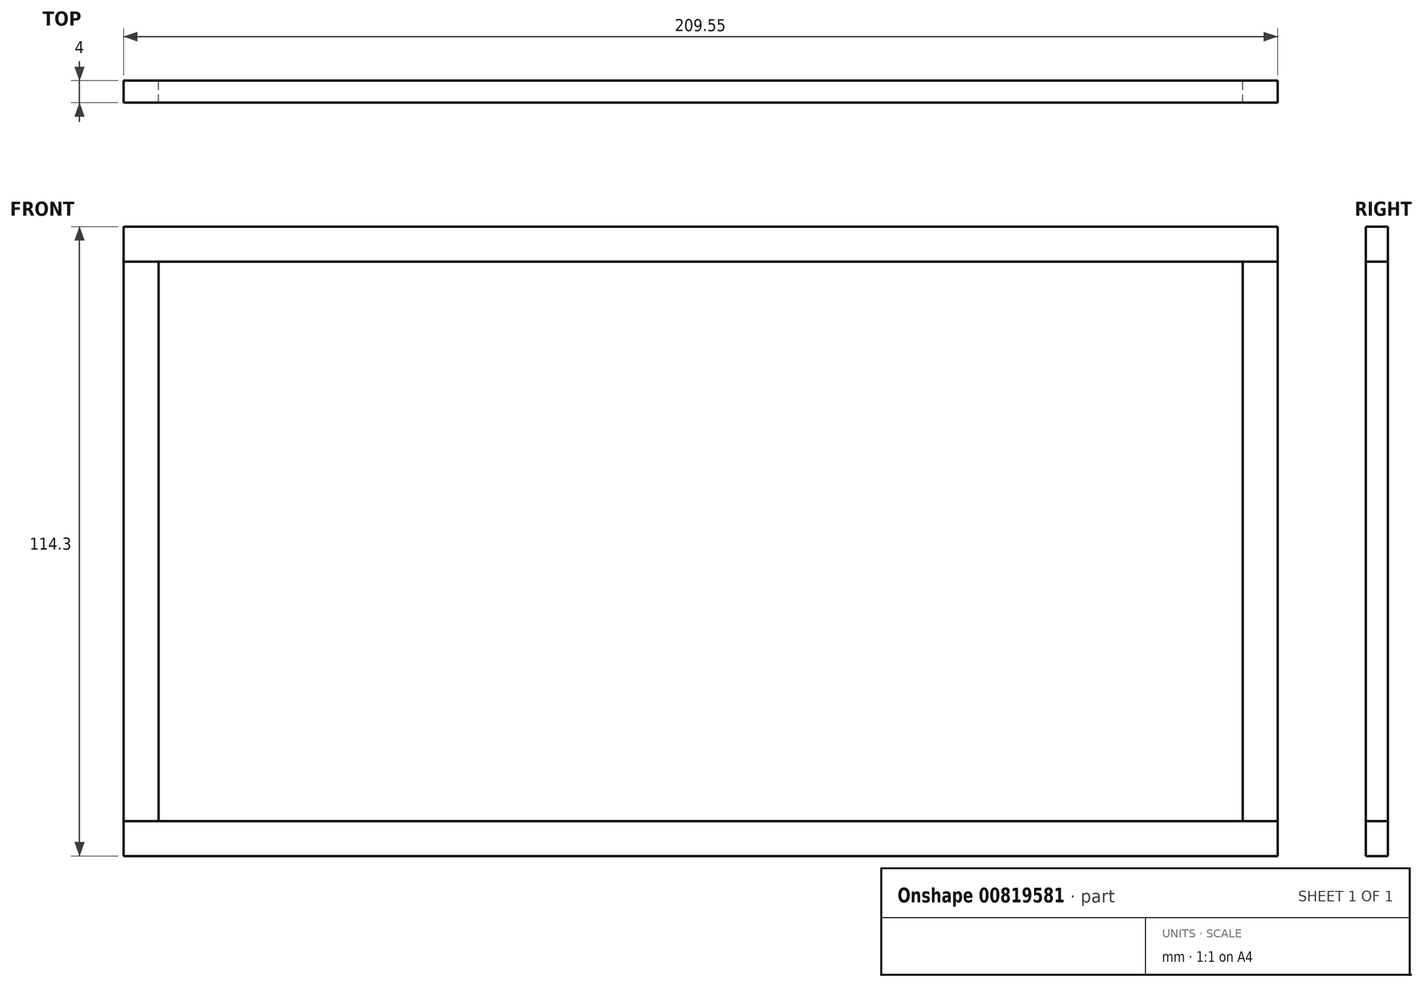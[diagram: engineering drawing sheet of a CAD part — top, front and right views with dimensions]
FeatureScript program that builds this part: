
annotation { "Feature Type Name" : "Feature", "Feature Type Description" : "" }
export const myFeature = defineFeature(function(context is Context, id is Id, definition is map)
    precondition{}
    {
        {
            assignVariable(context, id + "F0", {"name" : "depth", "anyValue" : 4});
        }
        {
            var Q0;
            Q0=qCreatedBy(makeId("Front.planeOp"),FACE);
            var sketch = newSketch(context, id + "F1", { "sketchPlane" : qUnion([Q0])});
            skLineSegment(sketch, "E0", {"start": v(-104.78, 0) * mm, "end": v(104.77, 0) * mm});
            skLineSegment(sketch, "E1", {"start": v(-104.78, 0) * mm, "end": v(-104.78, -114.3) * mm});
            skLineSegment(sketch, "E2", {"start": v(104.77, 0) * mm, "end": v(104.78, -114.3) * mm});
            skLineSegment(sketch, "E3", {"start": v(-104.78, -114.3) * mm, "end": v(104.78, -114.3) * mm});
            skLineSegment(sketch, "E4", {"start": v(-104.78, -6.35) * mm, "end": v(104.78, -6.35) * mm});
            skLineSegment(sketch, "E5", {"start": v(-104.78, -107.95) * mm, "end": v(104.78, -107.95) * mm});
            skLineSegment(sketch, "E6", {"start": v(-98.43, -6.35) * mm, "end": v(-98.42, -107.95) * mm});
            skLineSegment(sketch, "E7", {"start": v(98.42, -107.95) * mm, "end": v(98.42, -6.35) * mm});
            skLineSegment(sketch, "E8", {"start": v(0, 0) * mm, "end": v(0, -6.35) * mm, "construction": true});
            skLineSegment(sketch, "E9", {"start": v(-104.78, -57.15) * mm, "end": v(-98.43, -57.15) * mm, "construction": true});
            skLineSegment(sketch, "E10", {"start": v(98.42, -57.15) * mm, "end": v(104.77, -57.15) * mm, "construction": true});
            skPoint(sketch, "E10.startSnap0", {"position": v(104.77, -57.15) * mm});
            skLineSegment(sketch, "E11", {"start": v(0, -107.95) * mm, "end": v(0, -114.3) * mm, "construction": true});
            skLineSegment(sketch, "E12", {"start": v(-104.78, -57.15) * mm, "end": v(98.42, -57.15) * mm});
            skLineSegment(sketch, "E13.bottom", {"start": v(-79.38, -19.05) * mm, "end": v(-66.67, -19.05) * mm});
            skLineSegment(sketch, "E13.top", {"start": v(-79.38, -69.85) * mm, "end": v(-66.67, -69.85) * mm});
            skLineSegment(sketch, "E13.left", {"start": v(-79.38, -19.05) * mm, "end": v(-79.38, -69.85) * mm});
            skLineSegment(sketch, "E13.right", {"start": v(-66.67, -19.05) * mm, "end": v(-66.67, -69.85) * mm});
            skLineSegment(sketch, "E14.bottom", {"start": v(-6.02, -38.56) * mm, "end": v(6.68, -38.56) * mm});
            skLineSegment(sketch, "E14.top", {"start": v(-6.02, -89.36) * mm, "end": v(6.68, -89.36) * mm});
            skLineSegment(sketch, "E14.left", {"start": v(-6.02, -38.56) * mm, "end": v(-6.02, -89.36) * mm});
            skLineSegment(sketch, "E14.right", {"start": v(6.68, -38.56) * mm, "end": v(6.68, -89.36) * mm});
            skLineSegment(sketch, "E15.bottom", {"start": v(67.97, -38.1) * mm, "end": v(80.67, -38.1) * mm, "construction": true});
            skLineSegment(sketch, "E15.top", {"start": v(67.97, -88.9) * mm, "end": v(80.67, -88.9) * mm});
            skLineSegment(sketch, "E15.left", {"start": v(67.97, -38.1) * mm, "end": v(67.97, -88.9) * mm});
            skLineSegment(sketch, "E15.right", {"start": v(80.67, -38.1) * mm, "end": v(80.67, -88.9) * mm});
            skLineSegment(sketch, "E16", {"start": v(-79.38, -44.45) * mm, "end": v(-66.67, -44.45) * mm});
            skLineSegment(sketch, "E17", {"start": v(-6.02, -63.96) * mm, "end": v(6.68, -63.96) * mm});
            skLineSegment(sketch, "E18", {"start": v(67.97, -63.5) * mm, "end": v(80.67, -63.5) * mm});
            skLineSegment(sketch, "E19", {"start": v(-73.03, -44.45) * mm, "end": v(-73.03, -57.15) * mm, "construction": true});
            skLineSegment(sketch, "E20", {"start": v(0.33, -57.15) * mm, "end": v(0.33, -63.96) * mm, "construction": true});
            skLineSegment(sketch, "E21", {"start": v(74.32, -63.5) * mm, "end": v(74.32, -57.15) * mm, "construction": true});
            skSolve(sketch);
        }
        {
            var Q0;
            {var subQ5=sQuery(id+"F1.wireOp",EDGE,"E0");Q0=makeQuery(id+"F1.imprint","IMPRINT",FACE,{"disambiguationData":[TD([[makeQuery(id+"F1.imprint","IMPRINT",EDGE,{"derivedFrom":subQ5}),-1.0]])]});}
            var Q1;
            {var subQ0=sQuery(id+"F1.wireOp",EDGE,"E3");Q1=makeQuery(id+"F1.imprint","IMPRINT",FACE,{"disambiguationData":[TD([[makeQuery(id+"F1.imprint","IMPRINT",EDGE,{"derivedFrom":subQ0}),1.0]])]});}
            extrude(context, id + "F2", {"entities" : qUnion([Q0, Q1]), "endBound" : BoundingType.SYMMETRIC, "depth" : (getVariable(context, 'depth')) * mm, "offsetDistance" : 25.4 * mm});
        }
        {
            var Q0;
            {var subQ5=sQuery(id+"F1.wireOp",EDGE,"E6");Q0=makeQuery(id+"F1.imprint","IMPRINT",FACE,{"disambiguationData":[TD([[makeQuery(id+"F1.imprint","IMPRINT",EDGE,{"derivedFrom":subQ5}),-1.0]])]});}
            var Q1;
            {var subQ5=sQuery(id+"F1.wireOp",EDGE,"E7");Q1=makeQuery(id+"F1.imprint","IMPRINT",FACE,{"disambiguationData":[TD([[makeQuery(id+"F1.imprint","IMPRINT",EDGE,{"derivedFrom":subQ5}),-1.0]])]});}
            var Q2;
            Q2=makeQuery(id+"F2.opExtrude","CAP_FACE",FACE,{"disambiguationData":[OSD([sQuery(id+"F1.wireOp",EDGE,"E0"),sQuery(id+"F1.wireOp",EDGE,"E1"),sQuery(id+"F1.wireOp",EDGE,"E2"),sQuery(id+"F1.wireOp",EDGE,"E4")])],"isStart":false});
            var Q3;
            Q3=makeQuery(id+"F2.opExtrude","CAP_FACE",FACE,{"disambiguationData":[OSD([sQuery(id+"F1.wireOp",EDGE,"E0"),sQuery(id+"F1.wireOp",EDGE,"E1"),sQuery(id+"F1.wireOp",EDGE,"E2"),sQuery(id+"F1.wireOp",EDGE,"E4")])],"isStart":true});
            extrude(context, id + "F3", {"entities" : qUnion([Q0, Q1]), "endBound" : BoundingType.UP_TO_SURFACE, "depth" : 101.6 * mm, "endBoundEntityFace" : qUnion([Q2]), "offsetDistance" : 25.4 * mm, "hasSecondDirection" : true, "secondDirectionBound" : SecondDirectionBoundingType.UP_TO_SURFACE, "secondDirectionOppositeDirection" : true, "secondDirectionDepth" : 25.4 * mm, "secondDirectionBoundEntityFace" : qUnion([Q3])});
        }
    });
